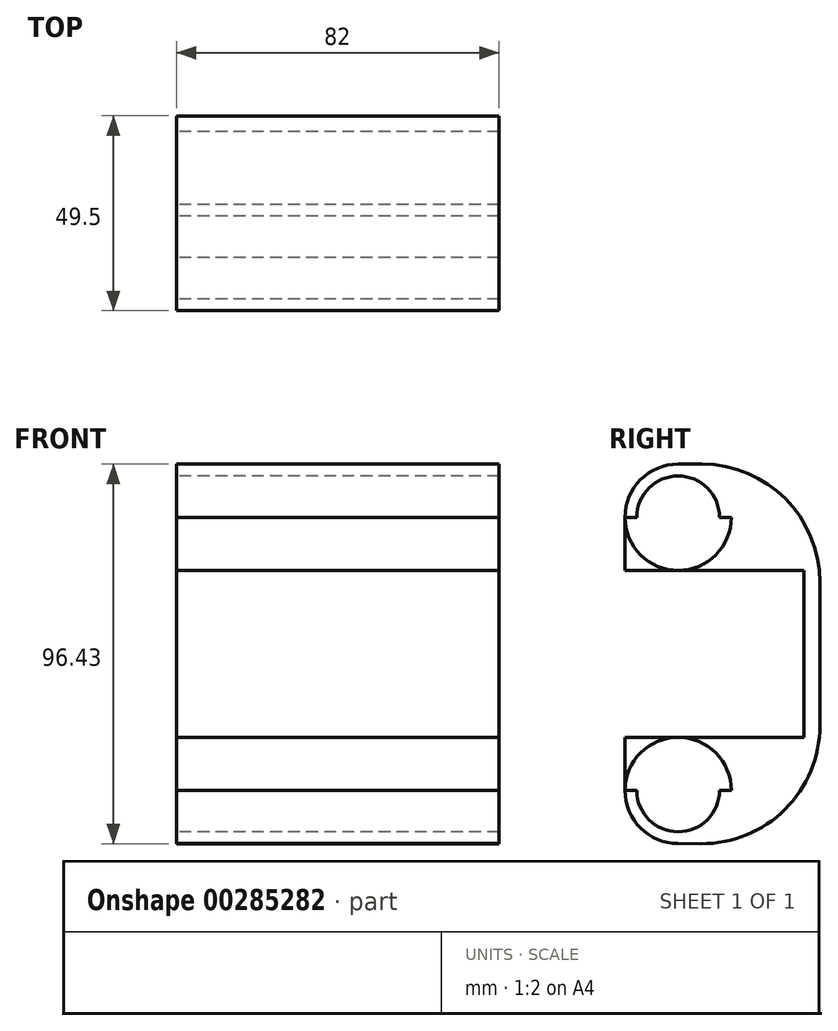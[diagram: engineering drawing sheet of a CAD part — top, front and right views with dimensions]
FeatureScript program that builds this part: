
annotation { "Feature Type Name" : "Feature", "Feature Type Description" : "" }
export const myFeature = defineFeature(function(context is Context, id is Id, definition is map)
    precondition{}
    {
        {
            var Q0;
            Q0=qCreatedBy(makeId("Right.planeOp"),FACE);
            var sketch = newSketch(context, id + "F0", { "sketchPlane" : qUnion([Q0])});
            skCircle(sketch, "E0", {"center": v(31, 13.71) * mm, "radius": 10.5 * mm});
            skLineSegment(sketch, "E1", {"start": v(31, 13.71) * mm, "end": v(31, 83.11) * mm});
            skCircle(sketch, "E2", {"center": v(31, 83.11) * mm, "radius": 10.5 * mm});
            skLineSegment(sketch, "E3.bottom", {"start": v(16, 69.61) * mm, "end": v(63, 69.61) * mm});
            skLineSegment(sketch, "E3.top", {"start": v(16, 27.21) * mm, "end": v(63, 27.21) * mm});
            skLineSegment(sketch, "E3.left", {"start": v(16, 69.61) * mm, "end": v(16, 27.21) * mm});
            skLineSegment(sketch, "E3.right", {"start": v(63, 69.61) * mm, "end": v(63, 27.21) * mm});
            skLineSegment(sketch, "E4", {"start": v(31, 69.61) * mm, "end": v(31, 72.61) * mm});
            skLineSegment(sketch, "E5", {"start": v(31, 27.21) * mm, "end": v(31, 24.21) * mm});
            skCircle(sketch, "E6", {"center": v(31, 13.71) * mm, "radius": 13.5 * mm});
            skCircle(sketch, "E7", {"center": v(31, 83.11) * mm, "radius": 13.5 * mm});
            skLineSegment(sketch, "E8", {"start": v(31, 83.11) * mm, "end": v(44.5, 83.11) * mm});
            skLineSegment(sketch, "E9", {"start": v(44.5, 83.11) * mm, "end": v(44.5, 13.71) * mm});
            skLineSegment(sketch, "E10", {"start": v(44.5, 13.71) * mm, "end": v(31, 13.71) * mm});
            skLineSegment(sketch, "E11", {"start": v(31, 83.11) * mm, "end": v(17.5, 83.11) * mm});
            skLineSegment(sketch, "E12", {"start": v(17.5, 83.11) * mm, "end": v(17.5, 13.71) * mm});
            skLineSegment(sketch, "E13", {"start": v(17.5, 13.71) * mm, "end": v(31, 13.71) * mm});
            skLineSegment(sketch, "E14.top", {"start": v(37, 96.61) * mm, "end": v(31, 96.61) * mm});
            skLineSegment(sketch, "E14.left", {"start": v(67, 30) * mm, "end": v(67, 66.61) * mm});
            skPoint(sketch, "E15.visualSharp", {"position": v(67, 96.61) * mm});
            skArc(sketch, "E15.filletArc", {"start": v(67, 66.61) * mm, "mid": v(58.22, 87.82) * mm, "end": v(37, 96.61) * mm});
            skPoint(sketch, "E16.visualSharp", {"position": v(67, 0) * mm});
            skLineSegment(sketch, "E17", {"start": v(31, 27.21) * mm, "end": v(31, 0.21) * mm});
            skLineSegment(sketch, "E18", {"start": v(31, 0.21) * mm, "end": v(36.83, 0.18) * mm});
            skLineSegment(sketch, "E19", {"start": v(67, 30.18) * mm, "end": v(67, 30) * mm});
            skArc(sketch, "E20.filletArc", {"start": v(36.83, 0.18) * mm, "mid": v(58.16, 8.9) * mm, "end": v(67, 30.18) * mm});
            skSolve(sketch);
        }
        {
            var Q0;
            {var subQ1=sQuery(id+"F0.wireOp",EDGE,"E3.bottom");var subQ3=sQuery(id+"F0.wireOp",EDGE,"E12");var subQ4=makeQuery(id+"F0.imprint","INTERSECT",VERTEX,{"derivedFrom":[subQ1,subQ3]});Q0=makeQuery(id+"F0.imprint","IMPRINT",FACE,{"disambiguationData":[TD([[makeQuery(id+"F0.imprint","IMPRINT",EDGE,{"disambiguationData":[TD([[subQ4,1.0]])],"derivedFrom":subQ3}),1.0]])]});}
            var Q1;
            {var subQ1=sQuery(id+"F0.wireOp",EDGE,"E3.top");var subQ3=sQuery(id+"F0.wireOp",EDGE,"E12");var subQ4=makeQuery(id+"F0.imprint","INTERSECT",VERTEX,{"derivedFrom":[subQ1,subQ3]});Q1=makeQuery(id+"F0.imprint","IMPRINT",FACE,{"disambiguationData":[TD([[makeQuery(id+"F0.imprint","IMPRINT",EDGE,{"disambiguationData":[TD([[subQ4,-1.0]])],"derivedFrom":subQ3}),1.0]])]});}
            var Q2;
            {var subQ0=sQuery(id+"F0.wireOp",EDGE,"E13");var subQ1=sQuery(id+"F0.wireOp",EDGE,"E0");var subQ2=makeQuery(id+"F0.imprint","INTERSECT",VERTEX,{"derivedFrom":[subQ1,subQ0]});Q2=makeQuery(id+"F0.imprint","IMPRINT",FACE,{"disambiguationData":[TD([[makeQuery(id+"F0.imprint","IMPRINT",EDGE,{"disambiguationData":[TD([[subQ2,-1.0]])],"derivedFrom":subQ1}),-1.0]])]});}
            var Q3;
            {var subQ0=sQuery(id+"F0.wireOp",EDGE,"E17");var subQ1=sQuery(id+"F0.wireOp",EDGE,"E0");var subQ2=makeQuery(id+"F0.imprint","INTERSECT",VERTEX,{"disambiguationData":[OD(0.0)],"derivedFrom":[subQ1,subQ0]});Q3=makeQuery(id+"F0.imprint","IMPRINT",FACE,{"disambiguationData":[TD([[makeQuery(id+"F0.imprint","IMPRINT",EDGE,{"disambiguationData":[TD([[subQ2,-1.0]])],"derivedFrom":subQ1}),-1.0]])]});}
            var Q4;
            {var subQ0=sQuery(id+"F0.wireOp",EDGE,"E10");var subQ1=sQuery(id+"F0.wireOp",EDGE,"E0");var subQ2=makeQuery(id+"F0.imprint","INTERSECT",VERTEX,{"derivedFrom":[subQ1,subQ0]});Q4=makeQuery(id+"F0.imprint","IMPRINT",FACE,{"disambiguationData":[TD([[makeQuery(id+"F0.imprint","IMPRINT",EDGE,{"disambiguationData":[TD([[subQ2,1.0]])],"derivedFrom":subQ1}),-1.0]])]});}
            var Q5;
            {var subQ0=sQuery(id+"F0.wireOp",EDGE,"E11");var subQ4=sQuery(id+"F0.wireOp",EDGE,"E2");var subQ5=makeQuery(id+"F0.imprint","INTERSECT",VERTEX,{"derivedFrom":[subQ4,subQ0]});Q5=makeQuery(id+"F0.imprint","IMPRINT",FACE,{"disambiguationData":[TD([[makeQuery(id+"F0.imprint","IMPRINT",EDGE,{"disambiguationData":[TD([[subQ5,1.0]])],"derivedFrom":subQ4}),-1.0]])]});}
            var Q6;
            {var subQ0=sQuery(id+"F0.wireOp",EDGE,"E4");Q6=makeQuery(id+"F0.imprint","IMPRINT",FACE,{"disambiguationData":[TD([[makeQuery(id+"F0.imprint","IMPRINT",EDGE,{"derivedFrom":subQ0}),1.0]])]});}
            var Q7;
            {var subQ10=sQuery(id+"F0.wireOp",EDGE,"E3.right");Q7=makeQuery(id+"F0.imprint","IMPRINT",FACE,{"disambiguationData":[TD([[makeQuery(id+"F0.imprint","IMPRINT",EDGE,{"derivedFrom":subQ10}),1.0]])]});}
            var Q8;
            {var subQ1=sQuery(id+"F0.wireOp",EDGE,"E3.top");var subQ3=sQuery(id+"F0.wireOp",EDGE,"E9");var subQ4=makeQuery(id+"F0.imprint","INTERSECT",VERTEX,{"derivedFrom":[subQ1,subQ3]});Q8=makeQuery(id+"F0.imprint","IMPRINT",FACE,{"disambiguationData":[TD([[makeQuery(id+"F0.imprint","IMPRINT",EDGE,{"disambiguationData":[TD([[subQ4,-1.0]])],"derivedFrom":subQ3}),-1.0]])]});}
            var Q9;
            {var subQ0=sQuery(id+"F0.wireOp",EDGE,"E17");var subQ1=sQuery(id+"F0.wireOp",EDGE,"E0");var subQ2=makeQuery(id+"F0.imprint","INTERSECT",VERTEX,{"disambiguationData":[OD(0.0)],"derivedFrom":[subQ1,subQ0]});Q9=makeQuery(id+"F0.imprint","IMPRINT",FACE,{"disambiguationData":[TD([[makeQuery(id+"F0.imprint","IMPRINT",EDGE,{"disambiguationData":[TD([[subQ2,1.0]])],"derivedFrom":subQ1}),-1.0]])]});}
            var Q10;
            {var subQ1=sQuery(id+"F0.wireOp",EDGE,"E3.bottom");var subQ3=sQuery(id+"F0.wireOp",EDGE,"E9");var subQ4=makeQuery(id+"F0.imprint","INTERSECT",VERTEX,{"derivedFrom":[subQ1,subQ3]});Q10=makeQuery(id+"F0.imprint","IMPRINT",FACE,{"disambiguationData":[TD([[makeQuery(id+"F0.imprint","IMPRINT",EDGE,{"disambiguationData":[TD([[subQ4,1.0]])],"derivedFrom":subQ3}),-1.0]])]});}
            var Q11;
            {var subQ0=sQuery(id+"F0.wireOp",EDGE,"E4");Q11=makeQuery(id+"F0.imprint","IMPRINT",FACE,{"disambiguationData":[TD([[makeQuery(id+"F0.imprint","IMPRINT",EDGE,{"derivedFrom":subQ0}),-1.0]])]});}
            extrude(context, id + "F1", {"entities" : qUnion([Q0, Q1, Q2, Q3, Q4, Q5, Q6, Q7, Q8, Q9, Q10, Q11]), "depth" : 82 * mm});
        }
    });
